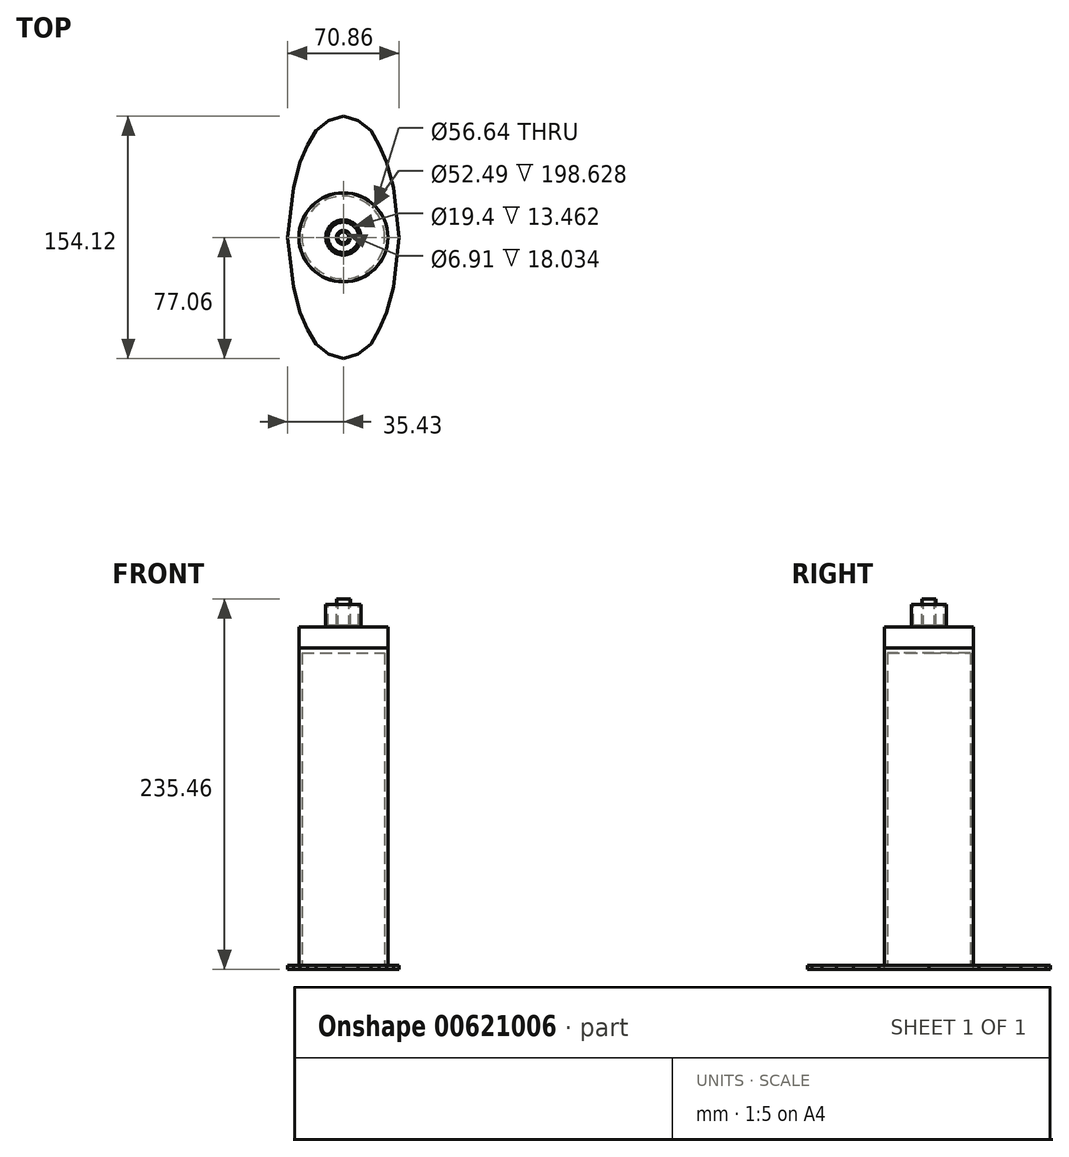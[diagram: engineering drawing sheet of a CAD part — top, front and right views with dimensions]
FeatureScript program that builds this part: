
annotation { "Feature Type Name" : "Feature", "Feature Type Description" : "" }
export const myFeature = defineFeature(function(context is Context, id is Id, definition is map)
    precondition{}
    {
        {
            var Q0;
            Q0=qCreatedBy(makeId("Top.planeOp"),FACE);
            var sketch = newSketch(context, id + "F0", { "sketchPlane" : qUnion([Q0])});
            skCircle(sketch, "E0", {"center": v(0, 0) * mm, "radius": 28.32 * mm});
            skSolve(sketch);
        }
        {
            var Q0;
            Q0=makeQuery(id+"F0.imprint","IMPRINT",FACE,{"disambiguationData":[TD([[makeQuery(id+"F0.imprint","IMPRINT",EDGE,{"derivedFrom":sQuery(id+"F0.wireOp",EDGE,"E0")}),1.0]])]});
            var Q1;
            Q1 = qSketchRegion(id + "Fne60ovAYDlkCra_1", true);
            extrude(context, id + "F1", {"entities" : qUnion([Q0, Q1]), "depth" : 141.22 * mm, "offsetDistance" : 25.4 * mm});
        }
        {
            var Q0;
            Q0=makeQuery(id+"F1.opExtrude","CAP_FACE",FACE,{"disambiguationData":[OSD([sQuery(id+"F0.wireOp",EDGE,"E0")])],"isStart":true});
            extrude(context, id + "F2", {"entities" : qUnion([Q0]), "operationType" : NewBodyOperationType.ADD, "depth" : 60.45 * mm, "offsetDistance" : 25.4 * mm});
        }
        {
            var Q0;
            Q0=makeQuery(id+"F2.opExtrude","CAP_FACE",FACE,{"disambiguationData":[OSD([sQuery(id+"F0.wireOp",EDGE,"E0")])],"isStart":false});
            var sketch = newSketch(context, id + "F3", { "sketchPlane" : qUnion([Q0])});
            skCircle(sketch, "E1", {"center": v(0, 0) * mm, "radius": 26.25 * mm});
            skSolve(sketch);
        }
        {
            var Q0;
            Q0 = qSketchRegion(id + "F3", true);
            extrude(context, id + "F4", {"entities" : qUnion([Q0]), "operationType" : NewBodyOperationType.REMOVE, "oppositeDirection" : true, "depth" : 198.63 * mm, "offsetDistance" : 25.4 * mm});
        }
        {
            var Q0;
            Q0=makeQuery(id+"F3.imprint","IMPRINT",FACE,{"disambiguationData":[TD([[makeQuery(id+"F3.imprint","IMPRINT",EDGE,{"derivedFrom":sQuery(id+"F3.wireOp",EDGE,"E1")}),-1.0]])]});
            var sketch = newSketch(context, id + "F5", { "sketchPlane" : qUnion([Q0])});
            skLineSegment(sketch, "E2", {"start": v(0, 77.06) * mm, "end": v(-9.47, 74.2) * mm});
            skLineSegment(sketch, "E3", {"start": v(-9.47, 74.2) * mm, "end": v(-17.46, 67.77) * mm});
            skLineSegment(sketch, "E4", {"start": v(-17.46, 67.77) * mm, "end": v(-22.67, 58.6) * mm});
            skLineSegment(sketch, "E5", {"start": v(-22.67, 58.6) * mm, "end": v(-27.5, 47.9) * mm});
            skLineSegment(sketch, "E6", {"start": v(-27.5, 47.9) * mm, "end": v(-31.77, 31.62) * mm});
            skLineSegment(sketch, "E7", {"start": v(-31.77, 31.62) * mm, "end": v(-35.43, 0) * mm});
            skLineSegment(sketch, "E8.MirrorCS", {"start": v(-31.77, -31.62) * mm, "end": v(-35.43, 0) * mm});
            skLineSegment(sketch, "E9.MirrorCS", {"start": v(-27.5, -47.9) * mm, "end": v(-31.77, -31.62) * mm});
            skLineSegment(sketch, "E10.MirrorCS", {"start": v(-22.67, -58.6) * mm, "end": v(-27.5, -47.9) * mm});
            skLineSegment(sketch, "E11.MirrorCS", {"start": v(-17.46, -67.77) * mm, "end": v(-22.67, -58.6) * mm});
            skLineSegment(sketch, "E12.MirrorCS", {"start": v(-9.47, -74.2) * mm, "end": v(-17.46, -67.77) * mm});
            skLineSegment(sketch, "E13.MirrorCS", {"start": v(0, -77.06) * mm, "end": v(-9.47, -74.2) * mm});
            skLineSegment(sketch, "E14.MirrorCS", {"start": v(0, -77.06) * mm, "end": v(9.47, -74.2) * mm});
            skLineSegment(sketch, "E15.MirrorCS", {"start": v(17.46, -67.77) * mm, "end": v(22.67, -58.6) * mm});
            skLineSegment(sketch, "E16.MirrorCS", {"start": v(9.47, -74.2) * mm, "end": v(17.46, -67.77) * mm});
            skLineSegment(sketch, "E17.MirrorCS", {"start": v(22.67, -58.6) * mm, "end": v(27.5, -47.9) * mm});
            skLineSegment(sketch, "E18.MirrorCS", {"start": v(27.5, -47.9) * mm, "end": v(31.77, -31.62) * mm});
            skLineSegment(sketch, "E19.MirrorCS", {"start": v(31.77, -31.62) * mm, "end": v(35.43, 0) * mm});
            skLineSegment(sketch, "E20.MirrorCS", {"start": v(31.77, 31.62) * mm, "end": v(35.43, 0) * mm});
            skLineSegment(sketch, "E21.MirrorCS", {"start": v(27.5, 47.9) * mm, "end": v(31.77, 31.62) * mm});
            skLineSegment(sketch, "E22.MirrorCS", {"start": v(22.67, 58.6) * mm, "end": v(27.5, 47.9) * mm});
            skLineSegment(sketch, "E23.MirrorCS", {"start": v(17.46, 67.77) * mm, "end": v(22.67, 58.6) * mm});
            skLineSegment(sketch, "E24.MirrorCS", {"start": v(9.47, 74.2) * mm, "end": v(17.46, 67.77) * mm});
            skLineSegment(sketch, "E25.MirrorCS", {"start": v(0, 77.06) * mm, "end": v(9.47, 74.2) * mm});
            skPoint(sketch, "E26.MirrorCS.end.orphan", {"position": v(0, -77.06) * mm});
            skPoint(sketch, "E26.MirrorCS.start.orphan", {"position": v(0, 0) * mm});
            skSolve(sketch);
        }
        {
            var Q0;
            Q0=makeQuery(id+"F5.imprint","IMPRINT",FACE,{"disambiguationData":[TD([[makeQuery(id+"F5.imprint","IMPRINT",EDGE,{"derivedFrom":sQuery(id+"F5.wireOp",EDGE,"E2")}),1.0]])]});
            extrude(context, id + "F6", {"entities" : qUnion([Q0]), "depth" : 2.54 * mm, "offsetDistance" : 25.4 * mm});
        }
        {
            var Q0;
            Q0=makeQuery(id+"F1.opExtrude","CAP_FACE",FACE,{"disambiguationData":[OSD([sQuery(id+"F0.wireOp",EDGE,"E0")])],"isStart":false});
            var sketch = newSketch(context, id + "F7", { "sketchPlane" : qUnion([Q0])});
            skCircle(sketch, "E27", {"center": v(0, 0) * mm, "radius": 28.23 * mm});
            skSolve(sketch);
        }
        {
            var Q0;
            Q0 = qSketchRegion(id + "F7", true);
            extrude(context, id + "F8", {"entities" : qUnion([Q0]), "operationType" : NewBodyOperationType.ADD, "depth" : 13.2 * mm, "offsetDistance" : 25.4 * mm});
        }
        {
            var Q0;
            Q0=makeQuery(id+"F8.opExtrude","CAP_FACE",FACE,{"disambiguationData":[OSD([sQuery(id+"F7.wireOp",EDGE,"E27")])],"isStart":false});
            var sketch = newSketch(context, id + "F9", { "sketchPlane" : qUnion([Q0])});
            skCircle(sketch, "E28", {"center": v(0, 0) * mm, "radius": 11.18 * mm});
            skSolve(sketch);
        }
        {
            var Q0;
            Q0=makeQuery(id+"F9.imprint","IMPRINT",FACE,{"disambiguationData":[TD([[makeQuery(id+"F9.imprint","IMPRINT",EDGE,{"derivedFrom":sQuery(id+"F9.wireOp",EDGE,"E28")}),1.0]])]});
            extrude(context, id + "F10", {"entities" : qUnion([Q0]), "operationType" : NewBodyOperationType.ADD, "depth" : 14.48 * mm, "offsetDistance" : 25.4 * mm});
        }
        {
            var Q0;
            Q0=makeQuery(id+"F10.opExtrude","CAP_FACE",FACE,{"disambiguationData":[OSD([sQuery(id+"F9.wireOp",EDGE,"E28")])],"isStart":false});
            var sketch = newSketch(context, id + "F11", { "sketchPlane" : qUnion([Q0])});
            skCircle(sketch, "E29", {"center": v(0, 0) * mm, "radius": 9.7 * mm});
            skSolve(sketch);
        }
        {
            var Q0;
            Q0=makeQuery(id+"F11.imprint","IMPRINT",FACE,{"disambiguationData":[TD([[makeQuery(id+"F11.imprint","IMPRINT",EDGE,{"derivedFrom":sQuery(id+"F11.wireOp",EDGE,"E29")}),1.0]])]});
            extrude(context, id + "F12", {"entities" : qUnion([Q0]), "operationType" : NewBodyOperationType.REMOVE, "oppositeDirection" : true, "depth" : 13.46 * mm, "offsetDistance" : 25.4 * mm});
        }
        {
            var Q0;
            Q0=makeQuery(id+"F10.opExtrude","CAP_FACE",FACE,{"disambiguationData":[OSD([sQuery(id+"F9.wireOp",EDGE,"E28")])],"isStart":false});
            var sketch = newSketch(context, id + "F13", { "sketchPlane" : qUnion([Q0])});
            skCircle(sketch, "E30", {"center": v(0, 0) * mm, "radius": 4.46 * mm});
            skSolve(sketch);
        }
        {
            var Q0;
            Q0=makeQuery(id+"F13.imprint","IMPRINT",FACE,{"disambiguationData":[TD([[makeQuery(id+"F13.imprint","IMPRINT",EDGE,{"derivedFrom":sQuery(id+"F13.wireOp",EDGE,"E30")}),1.0]])]});
            extrude(context, id + "F14", {"entities" : qUnion([Q0]), "operationType" : NewBodyOperationType.ADD, "oppositeDirection" : true, "depth" : 14.48 * mm, "offsetDistance" : 25.4 * mm});
        }
        {
            var Q0;
            Q0=makeQuery(id+"F14.opExtrude","CAP_FACE",FACE,{"disambiguationData":[OSD([sQuery(id+"F13.wireOp",EDGE,"E30")])],"isStart":true});
            extrude(context, id + "F15", {"entities" : qUnion([Q0]), "operationType" : NewBodyOperationType.ADD, "depth" : 3.56 * mm, "offsetDistance" : 25.4 * mm});
        }
        {
            var Q0;
            Q0=makeQuery(id+"F15.opExtrude","CAP_FACE",FACE,{"disambiguationData":[OSD([sQuery(id+"F13.wireOp",EDGE,"E30")])],"isStart":false});
            var sketch = newSketch(context, id + "F16", { "sketchPlane" : qUnion([Q0])});
            skCircle(sketch, "E31", {"center": v(0, 0) * mm, "radius": 3.46 * mm});
            skSolve(sketch);
        }
        {
            var Q0;
            Q0=makeQuery(id+"F16.imprint","IMPRINT",FACE,{"disambiguationData":[TD([[makeQuery(id+"F16.imprint","IMPRINT",EDGE,{"derivedFrom":sQuery(id+"F16.wireOp",EDGE,"E31")}),1.0]])]});
            extrude(context, id + "F17", {"entities" : qUnion([Q0]), "operationType" : NewBodyOperationType.REMOVE, "oppositeDirection" : true, "depth" : 18.03 * mm, "offsetDistance" : 25.4 * mm});
        }
    });
